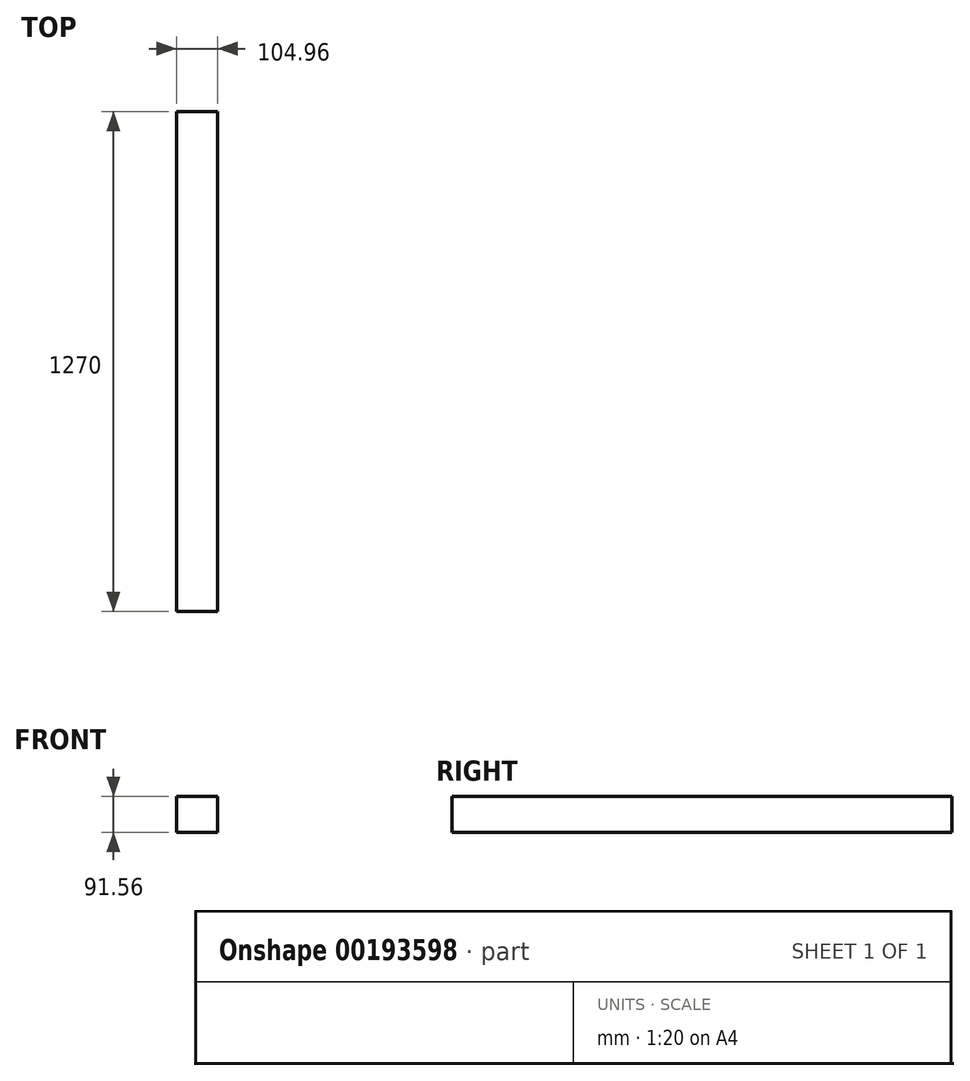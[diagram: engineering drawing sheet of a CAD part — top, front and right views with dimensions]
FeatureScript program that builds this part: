
annotation { "Feature Type Name" : "Feature", "Feature Type Description" : "" }
export const myFeature = defineFeature(function(context is Context, id is Id, definition is map)
    precondition{}
    {
        {
            var Q0;
            Q0=qCreatedBy(makeId("Front.planeOp"),FACE);
            var sketch = newSketch(context, id + "F0", { "sketchPlane" : qUnion([Q0])});
            skLineSegment(sketch, "E0.bottom", {"start": v(-52.48, 45.78) * mm, "end": v(52.48, 45.78) * mm});
            skLineSegment(sketch, "E0.top", {"start": v(-52.48, -45.78) * mm, "end": v(52.48, -45.78) * mm});
            skLineSegment(sketch, "E0.left", {"start": v(-52.48, 45.78) * mm, "end": v(-52.48, -45.78) * mm});
            skLineSegment(sketch, "E0.right", {"start": v(52.48, 45.78) * mm, "end": v(52.48, -45.78) * mm});
            skPoint(sketch, "E0.middle", {"position": v(0, 0) * mm});
            skSolve(sketch);
        }
        {
            var Q0;
            Q0 = qSketchRegion(id + "F0", true);
            extrude(context, id + "F1", {"entities" : qUnion([Q0]), "depth" : 1270 * mm});
        }
    });
